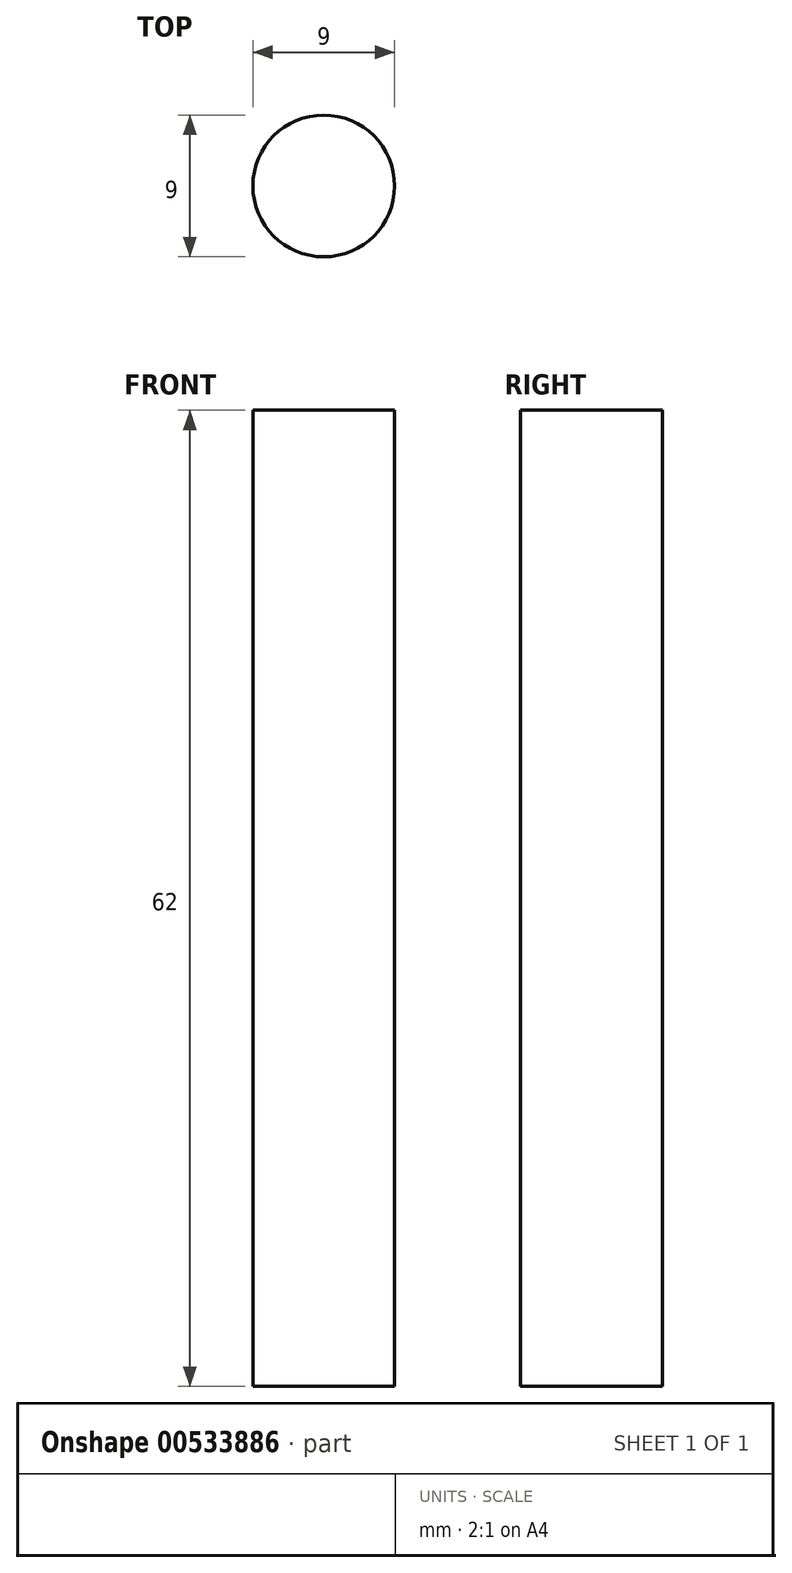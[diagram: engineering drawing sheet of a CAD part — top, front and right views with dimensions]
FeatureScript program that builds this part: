
annotation { "Feature Type Name" : "Feature", "Feature Type Description" : "" }
export const myFeature = defineFeature(function(context is Context, id is Id, definition is map)
    precondition{}
    {
        {
            var Q0;
            Q0=qCreatedBy(makeId("Top.planeOp"),FACE);
            var sketch = newSketch(context, id + "F0", { "sketchPlane" : qUnion([Q0])});
            skCircle(sketch, "E0", {"center": v(0, 0) * mm, "radius": 4.5 * mm});
            skSolve(sketch);
        }
        {
            var Q0;
            Q0=makeQuery(id+"F0.imprint","IMPRINT",FACE,{"disambiguationData":[TD([[makeQuery(id+"F0.imprint","IMPRINT",EDGE,{"derivedFrom":sQuery(id+"F0.wireOp",EDGE,"E0")}),1.0]])]});
            extrude(context, id + "F1", {"entities" : qUnion([Q0]), "depth" : 62 * mm, "offsetDistance" : 25 * mm});
        }
    });
